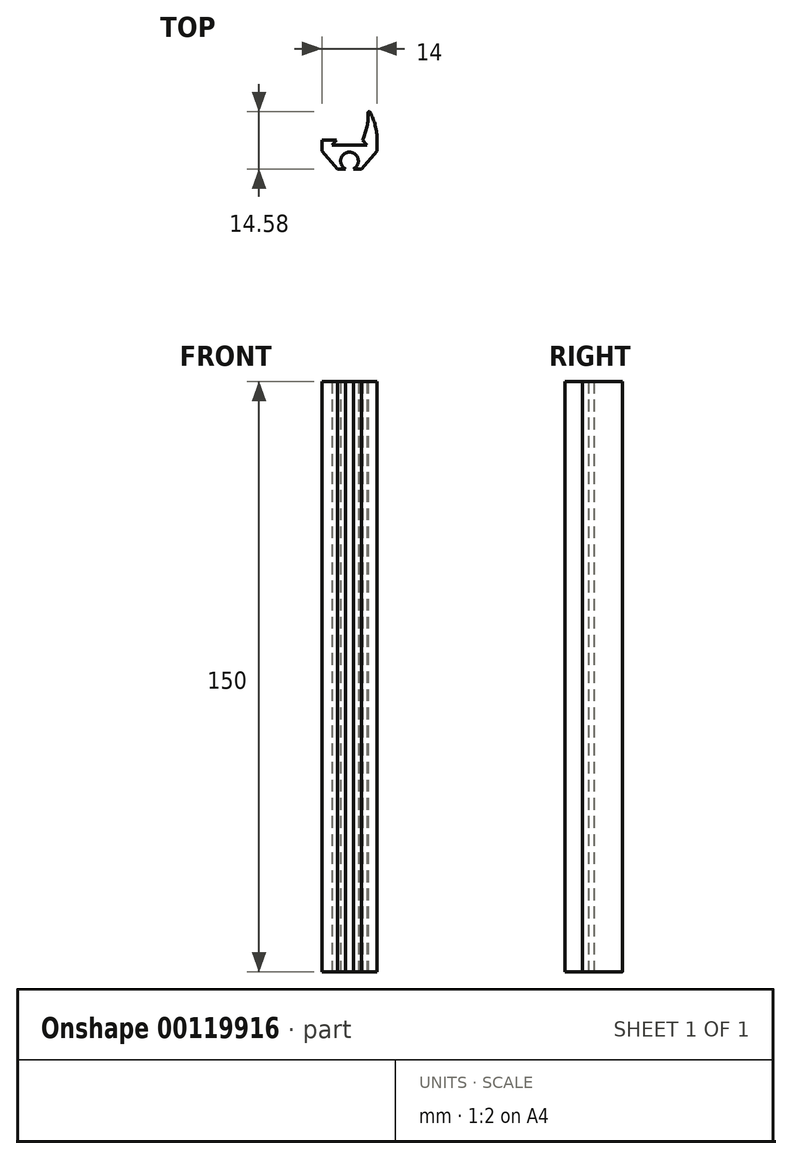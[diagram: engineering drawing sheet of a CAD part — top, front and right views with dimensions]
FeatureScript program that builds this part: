
annotation { "Feature Type Name" : "Feature", "Feature Type Description" : "" }
export const myFeature = defineFeature(function(context is Context, id is Id, definition is map)
    precondition{}
    {
        {
            var Q0;
            Q0=qCreatedBy(makeId("Top.planeOp"),FACE);
            var sketch = newSketch(context, id + "F0", { "sketchPlane" : qUnion([Q0])});
            skLineSegment(sketch, "E0.bottom", {"start": v(7, 4) * mm, "end": v(-7, 4) * mm});
            skLineSegment(sketch, "E0.top", {"start": v(7, 2.5) * mm, "end": v(-7, 2.5) * mm});
            skLineSegment(sketch, "E0.left", {"start": v(7, 4) * mm, "end": v(7, 2.5) * mm});
            skLineSegment(sketch, "E0.right", {"start": v(-7, 4) * mm, "end": v(-7, 2.5) * mm});
            skPoint(sketch, "E0.middle", {"position": v(0, 3.25) * mm});
            skLineSegment(sketch, "E1", {"start": v(0, 11.45) * mm, "end": v(0, -20.15) * mm, "construction": true});
            skArc(sketch, "E2", {"start": v(1, -2.02) * mm, "mid": v(0, 2.25) * mm, "end": v(-1, -2.02) * mm});
            skLineSegment(sketch, "E3", {"start": v(-1, -2.02) * mm, "end": v(-3, -2.02) * mm});
            skLineSegment(sketch, "E4", {"start": v(-3, -2.02) * mm, "end": v(-7, 2.5) * mm});
            skLineSegment(sketch, "E5", {"start": v(1, -2.02) * mm, "end": v(3, -2.02) * mm});
            skLineSegment(sketch, "E6", {"start": v(3, -2.02) * mm, "end": v(7, 2.5) * mm});
            skLineSegment(sketch, "E7", {"start": v(-4.5, 4) * mm, "end": v(-3.34, 5.38) * mm});
            skLineSegment(sketch, "E8", {"start": v(-3.34, 5.38) * mm, "end": v(-7, 5.38) * mm});
            skLineSegment(sketch, "E9", {"start": v(-7, 5.38) * mm, "end": v(-7, 4) * mm});
            skLineSegment(sketch, "E10.MirrorCS", {"start": v(7, 5.38) * mm, "end": v(7, 4) * mm});
            skLineSegment(sketch, "E11.MirrorCS", {"start": v(4.5, 4) * mm, "end": v(3.34, 5.38) * mm});
            skLineSegment(sketch, "E12.MirrorCS", {"start": v(3.34, 5.38) * mm, "end": v(7, 5.38) * mm});
            skArc(sketch, "E13", {"start": v(7, 5.38) * mm, "mid": v(6.55, 9.02) * mm, "end": v(5.21, 12.43) * mm});
            skArc(sketch, "E14", {"start": v(3.34, 5.38) * mm, "mid": v(4.43, 8.76) * mm, "end": v(4.74, 12.3) * mm});
            skPoint(sketch, "E15.visualSharp", {"position": v(4.68, 13.33) * mm});
            skArc(sketch, "E15.filletArc", {"start": v(5.21, 12.43) * mm, "mid": v(4.93, 12.55) * mm, "end": v(4.74, 12.3) * mm});
            skSolve(sketch);
        }
        {
            var Q0;
            Q0=qSketchRegion(id+"F0",true);
            extrude(context, id + "F1", {"entities" : qUnion([Q0]), "depth" : 150 * mm});
        }
    });
